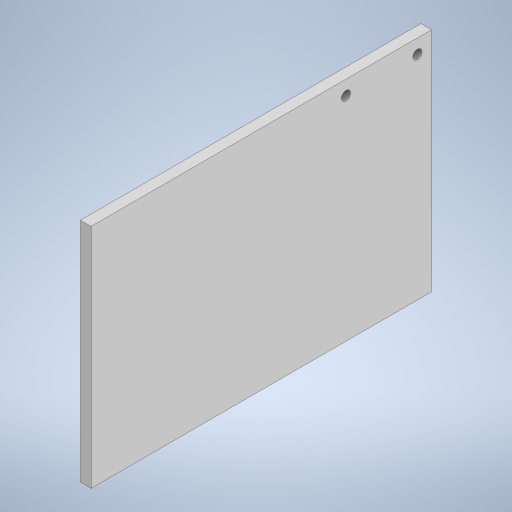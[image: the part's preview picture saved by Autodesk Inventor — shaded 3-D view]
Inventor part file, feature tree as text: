
AUTODESK INVENTOR PART (.ipt)
format: ipt  version: 2024.2 (Build 282272000, 272)  size: 200,192 bytes
history: native  units: in
note: dims shown in document units (in); Inventor stores cm internally (conversion verified against a paired STEP export)
features: extrude x2, sketch x2
ambient origin geometry x8: Origin, YZ Plane, XZ Plane, XY Plane, X Axis, Y Axis, Z Axis, Center Point
bodies: Solid1 (feature_tree)
feature tree (4):
  extrude  "Extrusion1"  Depth=6.0in
  extrude  "Extrusion2"  Depth=0.1875in
  sketch  "Sketch1"  dims[d0=4.0in d1=6.0in]
  sketch  "Sketch3"  dims[d2=0.1875in d3=0.0in d4=1.26in d5=0.157in d6=0.157in d7=0.25in d8=0.25in d9=0.25in d10=0.1875in d11=0.0in]
